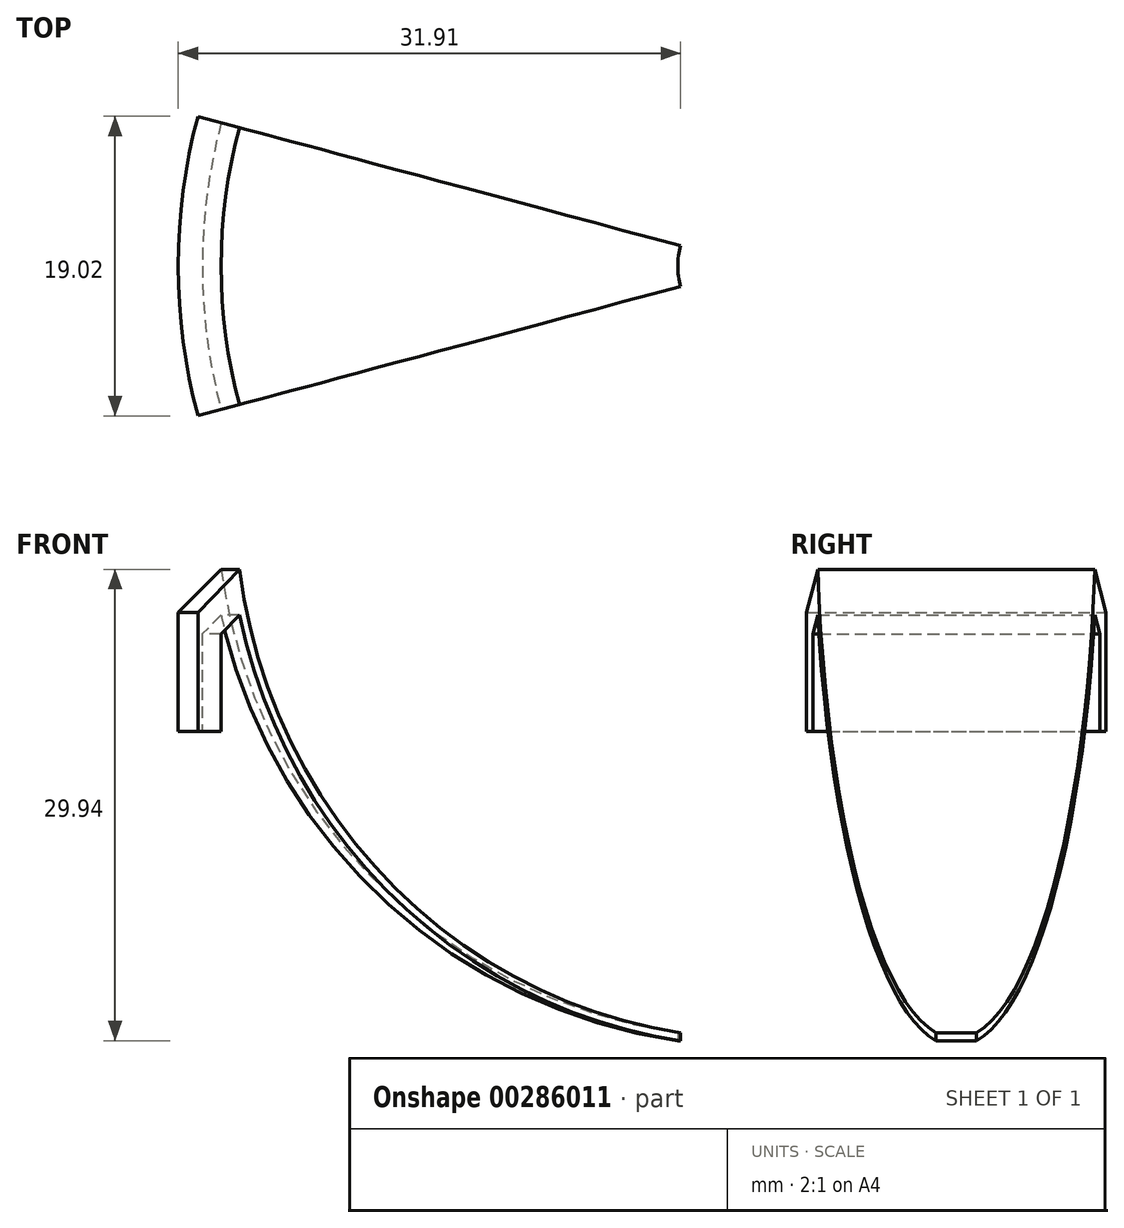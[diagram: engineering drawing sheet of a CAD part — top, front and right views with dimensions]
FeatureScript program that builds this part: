
annotation { "Feature Type Name" : "Feature", "Feature Type Description" : "" }
export const myFeature = defineFeature(function(context is Context, id is Id, definition is map)
    precondition{}
    {
        {
            var Q0;
            Q0=qCreatedBy(makeId("Front.planeOp"),FACE);
            var sketch = newSketch(context, id + "F0", { "sketchPlane" : qUnion([Q0])});
            skArc(sketch, "E0", {"start": v(2.88, 39.38) * mm, "mid": v(14.27, 18.09) * mm, "end": v(36.88, 9.58) * mm});
            skArc(sketch, "E1", {"start": v(2.88, 33.68) * mm, "mid": v(15.7, 15.48) * mm, "end": v(36.88, 8.58) * mm});
            skLineSegment(sketch, "E2", {"start": v(36.88, 9.58) * mm, "end": v(36.88, 8.58) * mm, "construction": true});
            skLineSegment(sketch, "E3", {"start": v(2.88, 39.38) * mm, "end": v(-0.13, 39.38) * mm, "construction": true});
            skLineSegment(sketch, "E4", {"start": v(0, 28.93) * mm, "end": v(1.75, 28.93) * mm});
            skLineSegment(sketch, "E5", {"start": v(1.75, 28.93) * mm, "end": v(1.75, 33.68) * mm});
            skLineSegment(sketch, "E6", {"start": v(-0.13, 28.93) * mm, "end": v(0, 28.93) * mm, "construction": true});
            skLineSegment(sketch, "E7", {"start": v(1.75, 28.93) * mm, "end": v(1.88, 28.93) * mm, "construction": true});
            skLineSegment(sketch, "E8", {"start": v(0, 28.93) * mm, "end": v(0, 39.38) * mm});
            skLineSegment(sketch, "E9", {"start": v(0, 39.38) * mm, "end": v(0, 36.5) * mm, "construction": true});
            skLineSegment(sketch, "E10", {"start": v(0, 36.5) * mm, "end": v(2.88, 39.38) * mm});
            skLineSegment(sketch, "E11", {"start": v(2.88, 39.38) * mm, "end": v(2.88, 33.68) * mm, "construction": true});
            skLineSegment(sketch, "E12", {"start": v(1.75, 33.68) * mm, "end": v(2.88, 33.68) * mm});
            skLineSegment(sketch, "E13", {"start": v(36.88, 8.58) * mm, "end": v(36.88, 43.88) * mm, "construction": true});
            skLineSegment(sketch, "E14", {"start": v(36.88, 8.58) * mm, "end": v(36.88, -38.27) * mm, "construction": true});
            skLineSegment(sketch, "E15", {"start": v(31.88, 8.9) * mm, "end": v(31.88, 9.95) * mm});
            skArc(sketch, "E16", {"start": v(3, 65.76) * mm, "mid": v(14.4, 44.47) * mm, "end": v(37, 35.97) * mm});
            skLineSegment(sketch, "E17", {"start": v(37, 35.97) * mm, "end": v(37, 34.97) * mm, "construction": true});
            skLineSegment(sketch, "E18", {"start": v(3, 65.76) * mm, "end": v(0, 65.76) * mm, "construction": true});
            skLineSegment(sketch, "E19", {"start": v(0.12, 55.32) * mm, "end": v(1.87, 55.32) * mm});
            skLineSegment(sketch, "E20", {"start": v(1.87, 55.32) * mm, "end": v(1.87, 60.07) * mm});
            skLineSegment(sketch, "E21", {"start": v(0, 55.32) * mm, "end": v(0.12, 55.32) * mm, "construction": true});
            skLineSegment(sketch, "E22", {"start": v(1.87, 55.32) * mm, "end": v(2, 55.32) * mm, "construction": true});
            skLineSegment(sketch, "E23", {"start": v(0.12, 55.32) * mm, "end": v(0.12, 65.76) * mm});
            skLineSegment(sketch, "E24", {"start": v(0.12, 65.76) * mm, "end": v(0.12, 62.89) * mm, "construction": true});
            skLineSegment(sketch, "E25", {"start": v(0.12, 62.89) * mm, "end": v(3, 65.76) * mm});
            skLineSegment(sketch, "E26", {"start": v(3, 65.76) * mm, "end": v(3, 60.07) * mm, "construction": true});
            skLineSegment(sketch, "E27", {"start": v(1.87, 60.07) * mm, "end": v(3, 60.07) * mm});
            skLineSegment(sketch, "E28", {"start": v(37, 34.97) * mm, "end": v(37, 70.26) * mm, "construction": true});
            skLineSegment(sketch, "E29", {"start": v(32, 35.3) * mm, "end": v(32, 36.33) * mm});
            skLineSegment(sketch, "E30", {"start": v(3, 61.97) * mm, "end": v(1.87, 61.97) * mm, "construction": true});
            skLineSegment(sketch, "E31", {"start": v(1.87, 61.97) * mm, "end": v(1.87, 60.07) * mm});
            skArc(sketch, "E32.trimOffspring", {"start": v(3, 61.97) * mm, "mid": v(15.38, 42.74) * mm, "end": v(37, 35.27) * mm});
            skArc(sketch, "E33", {"start": v(3, 7.25) * mm, "mid": v(14.4, -14.05) * mm, "end": v(37, -22.55) * mm});
            skLineSegment(sketch, "E34", {"start": v(37, -22.55) * mm, "end": v(37, -23.55) * mm, "construction": true});
            skLineSegment(sketch, "E35", {"start": v(3, 7.25) * mm, "end": v(0, 7.25) * mm, "construction": true});
            skLineSegment(sketch, "E36", {"start": v(0.13, -3.2) * mm, "end": v(1.88, -3.2) * mm, "construction": true});
            skLineSegment(sketch, "E37", {"start": v(1.88, -3.2) * mm, "end": v(1.88, 1.55) * mm, "construction": true});
            skLineSegment(sketch, "E38", {"start": v(0, -3.2) * mm, "end": v(0.13, -3.2) * mm, "construction": true});
            skLineSegment(sketch, "E39", {"start": v(1.88, -3.2) * mm, "end": v(2, -3.2) * mm, "construction": true});
            skLineSegment(sketch, "E40", {"start": v(0.13, -3.2) * mm, "end": v(0.13, 7.25) * mm, "construction": true});
            skLineSegment(sketch, "E41", {"start": v(0.13, 7.25) * mm, "end": v(0.13, 4.37) * mm, "construction": true});
            skLineSegment(sketch, "E42", {"start": v(0.12, 4.37) * mm, "end": v(3, 7.25) * mm});
            skLineSegment(sketch, "E43", {"start": v(3, 7.25) * mm, "end": v(3, 1.55) * mm, "construction": true});
            skLineSegment(sketch, "E44", {"start": v(1.88, 1.55) * mm, "end": v(3, 1.55) * mm});
            skLineSegment(sketch, "E45", {"start": v(37, -23.55) * mm, "end": v(37, 11.75) * mm, "construction": true});
            skLineSegment(sketch, "E46", {"start": v(32, -23.22) * mm, "end": v(32, -22.18) * mm});
            skArc(sketch, "E47.trimOffspring", {"start": v(3, 4.35) * mm, "mid": v(15.17, -15.35) * mm, "end": v(37, -23.05) * mm});
            skLineSegment(sketch, "E48", {"start": v(3, 4.35) * mm, "end": v(2.44, 4.35) * mm});
            skLineSegment(sketch, "E49", {"start": v(2.44, 4.35) * mm, "end": v(1.88, 4.35) * mm, "construction": true});
            skArc(sketch, "E50", {"start": v(3, -25.83) * mm, "mid": v(14.4, -47.12) * mm, "end": v(37, -55.62) * mm});
            skLineSegment(sketch, "E51", {"start": v(37, -55.62) * mm, "end": v(37, -56.62) * mm, "construction": true});
            skLineSegment(sketch, "E52", {"start": v(3, -25.83) * mm, "end": v(0, -25.83) * mm, "construction": true});
            skLineSegment(sketch, "E53", {"start": v(0.13, -36.28) * mm, "end": v(1.88, -36.28) * mm});
            skLineSegment(sketch, "E54", {"start": v(1.88, -36.28) * mm, "end": v(1.88, -31.53) * mm, "construction": true});
            skLineSegment(sketch, "E55", {"start": v(0, -36.28) * mm, "end": v(0.13, -36.28) * mm, "construction": true});
            skLineSegment(sketch, "E56", {"start": v(1.88, -36.28) * mm, "end": v(2, -36.28) * mm, "construction": true});
            skLineSegment(sketch, "E57", {"start": v(0.13, -36.28) * mm, "end": v(0.13, -25.83) * mm, "construction": true});
            skLineSegment(sketch, "E58", {"start": v(0.13, -25.83) * mm, "end": v(0.13, -28.7) * mm, "construction": true});
            skLineSegment(sketch, "E59", {"start": v(0.12, -28.7) * mm, "end": v(3, -25.83) * mm});
            skLineSegment(sketch, "E60", {"start": v(3, -25.83) * mm, "end": v(3, -31.53) * mm, "construction": true});
            skLineSegment(sketch, "E61", {"start": v(1.88, -31.53) * mm, "end": v(3, -31.53) * mm});
            skLineSegment(sketch, "E62", {"start": v(37, -56.62) * mm, "end": v(37, -21.33) * mm, "construction": true});
            skLineSegment(sketch, "E63", {"start": v(32, -56.3) * mm, "end": v(32, -55.26) * mm});
            skArc(sketch, "E64.0", {"start": v(3, -30.23) * mm, "mid": v(15.53, -49.15) * mm, "end": v(37, -56.47) * mm});
            skLineSegment(sketch, "E65", {"start": v(3, -30.23) * mm, "end": v(1.88, -30.23) * mm});
            skLineSegment(sketch, "E66", {"start": v(1.88, -30.23) * mm, "end": v(1.88, -31.53) * mm});
            skLineSegment(sketch, "E67", {"start": v(3, -30.23) * mm, "end": v(1.6, -30.23) * mm});
            skLineSegment(sketch, "E68", {"start": v(1.6, -30.23) * mm, "end": v(1.6, -36.28) * mm});
            skLineSegment(sketch, "E69", {"start": v(0.13, -36.28) * mm, "end": v(0.33, -36.28) * mm});
            skLineSegment(sketch, "E70", {"start": v(0.33, -36.28) * mm, "end": v(0.32, -28.5) * mm});
            skLineSegment(sketch, "E71", {"start": v(1.6, 0.62) * mm, "end": v(1.6, -3.2) * mm, "construction": true});
            skLineSegment(sketch, "E72", {"start": v(0.27, -3.2) * mm, "end": v(0.27, 4.52) * mm});
            skLineSegment(sketch, "E73", {"start": v(1.6, -3.05) * mm, "end": v(0.27, -3.05) * mm});
            skLineSegment(sketch, "E74", {"start": v(1.87, 61.97) * mm, "end": v(1.87, 60.85) * mm});
            skLineSegment(sketch, "E75", {"start": v(1.87, 60.85) * mm, "end": v(3, 61.97) * mm});
            skLineSegment(sketch, "E76", {"start": v(1.6, 0.62) * mm, "end": v(1.6, 4.35) * mm, "construction": true});
            skPoint(sketch, "E76.endSnap0", {"position": v(2.16, 4.35) * mm});
            skLineSegment(sketch, "E77", {"start": v(1.6, 4.35) * mm, "end": v(3, 4.35) * mm, "construction": true});
            skLineSegment(sketch, "E78", {"start": v(1.6, 4.35) * mm, "end": v(1.6, 2.95) * mm, "construction": true});
            skLineSegment(sketch, "E79", {"start": v(3, 4.35) * mm, "end": v(1.6, 2.95) * mm});
            skLineSegment(sketch, "E80", {"start": v(1.6, 2.95) * mm, "end": v(1.6, 0.62) * mm});
            skLineSegment(sketch, "E81", {"start": v(1.6, -3.05) * mm, "end": v(1.8, -3.05) * mm});
            skLineSegment(sketch, "E82", {"start": v(1.8, -3.05) * mm, "end": v(1.8, 3.15) * mm});
            skSolve(sketch);
        }
        {
            var Q0;
            {var subQ7=sQuery(id+"F0.wireOp",EDGE,"E73");Q0=makeQuery(id+"F0.imprint","IMPRINT",FACE,{"disambiguationData":[TD([[makeQuery(id+"F0.imprint","IMPRINT",EDGE,{"derivedFrom":subQ7}),-1.0]])]});}
            var Q1;
            Q1=sQuery(id+"F0.wireOp",EDGE,"E62");
            revolve(context, id + "F1", {"entities" : qUnion([Q0]), "axis" : qUnion([Q1]), "revolveType" : RevolveType.SYMMETRIC, "angle" : 30 * degree});
        }
    });
